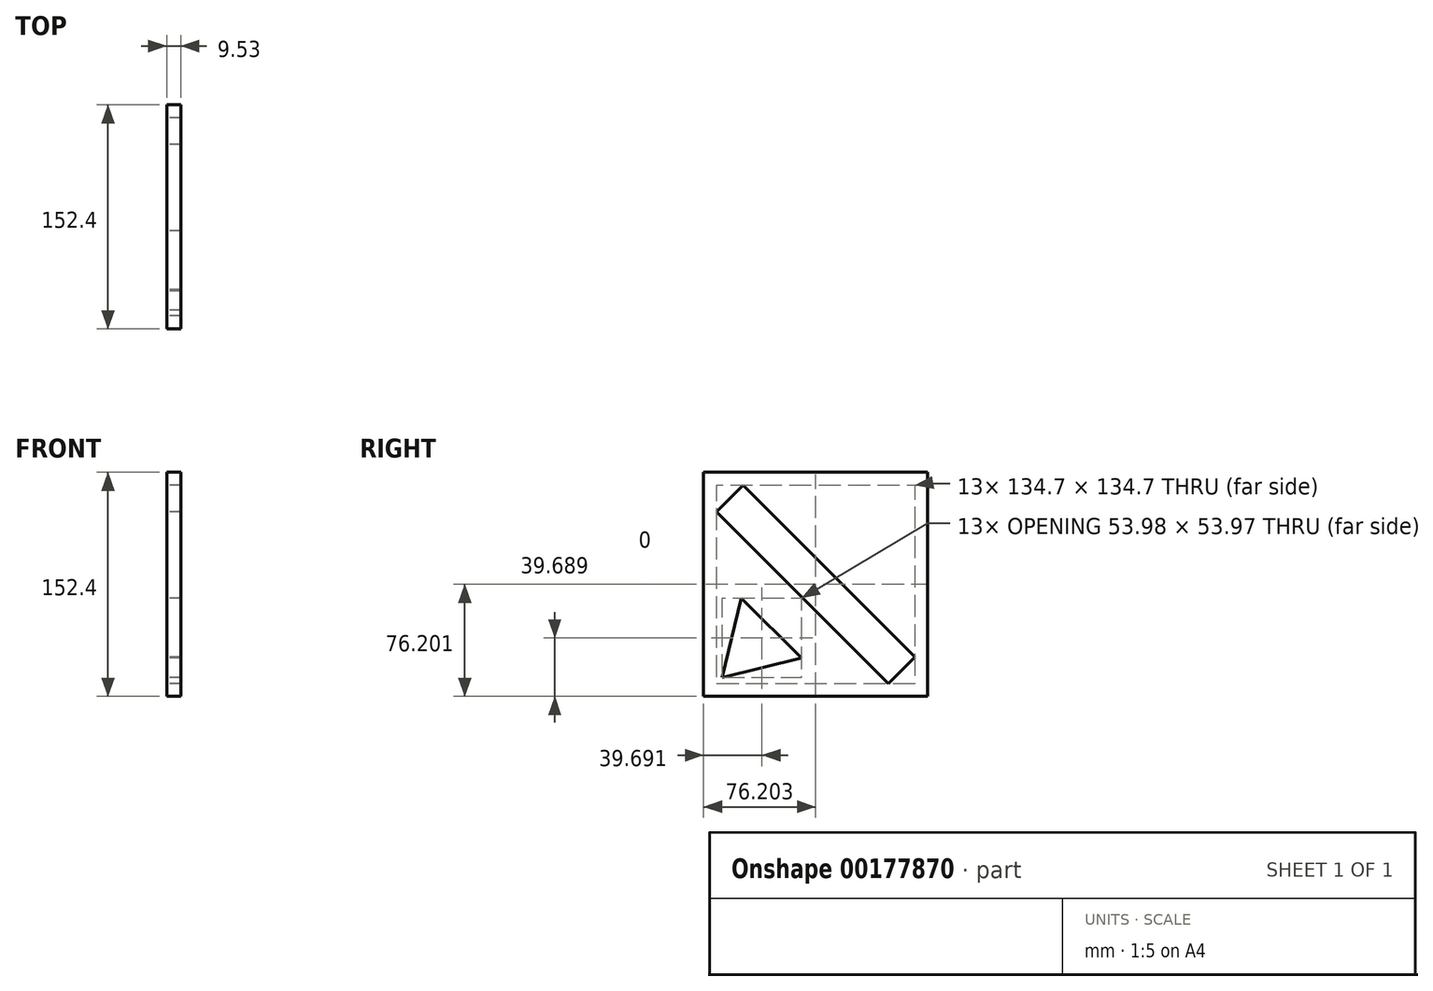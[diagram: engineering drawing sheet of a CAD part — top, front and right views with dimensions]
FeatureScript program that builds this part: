
annotation { "Feature Type Name" : "Feature", "Feature Type Description" : "" }
export const myFeature = defineFeature(function(context is Context, id is Id, definition is map)
    precondition{}
    {
        {
            var Q0;
            Q0=qCreatedBy(makeId("Right.planeOp"),FACE);
            var sketch = newSketch(context, id + "F0", { "sketchPlane" : qUnion([Q0])});
            skLineSegment(sketch, "E0", {"start": v(-63.29, -63.68) * mm, "end": v(-50.32, -9.7) * mm});
            skLineSegment(sketch, "E1", {"start": v(-50.32, -9.7) * mm, "end": v(-9.31, -50.35) * mm});
            skLineSegment(sketch, "E2", {"start": v(-9.31, -50.35) * mm, "end": v(-63.29, -63.68) * mm});
            skLineSegment(sketch, "E3.bottom", {"start": v(-49.18, 67.17) * mm, "end": v(-67.14, 49.21) * mm});
            skLineSegment(sketch, "E3.top", {"start": v(67.57, -49.57) * mm, "end": v(49.6, -67.53) * mm});
            skPoint(sketch, "E3.middle", {"position": v(0.21, -0.18) * mm});
            skLineSegment(sketch, "E4", {"start": v(-49.18, 67.17) * mm, "end": v(67.57, -49.57) * mm});
            skLineSegment(sketch, "E5", {"start": v(49.6, -67.53) * mm, "end": v(-67.14, 49.21) * mm});
            skLineSegment(sketch, "E6.bottom", {"start": v(-75.99, 76.02) * mm, "end": v(76.41, 76.02) * mm});
            skLineSegment(sketch, "E6.top", {"start": v(-75.99, -76.38) * mm, "end": v(76.41, -76.38) * mm});
            skLineSegment(sketch, "E6.left", {"start": v(-75.99, 76.02) * mm, "end": v(-75.99, -76.38) * mm});
            skLineSegment(sketch, "E6.right", {"start": v(76.41, 76.02) * mm, "end": v(76.41, -76.38) * mm});
            skSolve(sketch);
        }
        {
            var Q0;
            Q0 = qSketchRegion(id + "F0", true);
            extrude(context, id + "F1", {"entities" : qUnion([Q0]), "depth" : 9.52 * mm});
        }
    });
